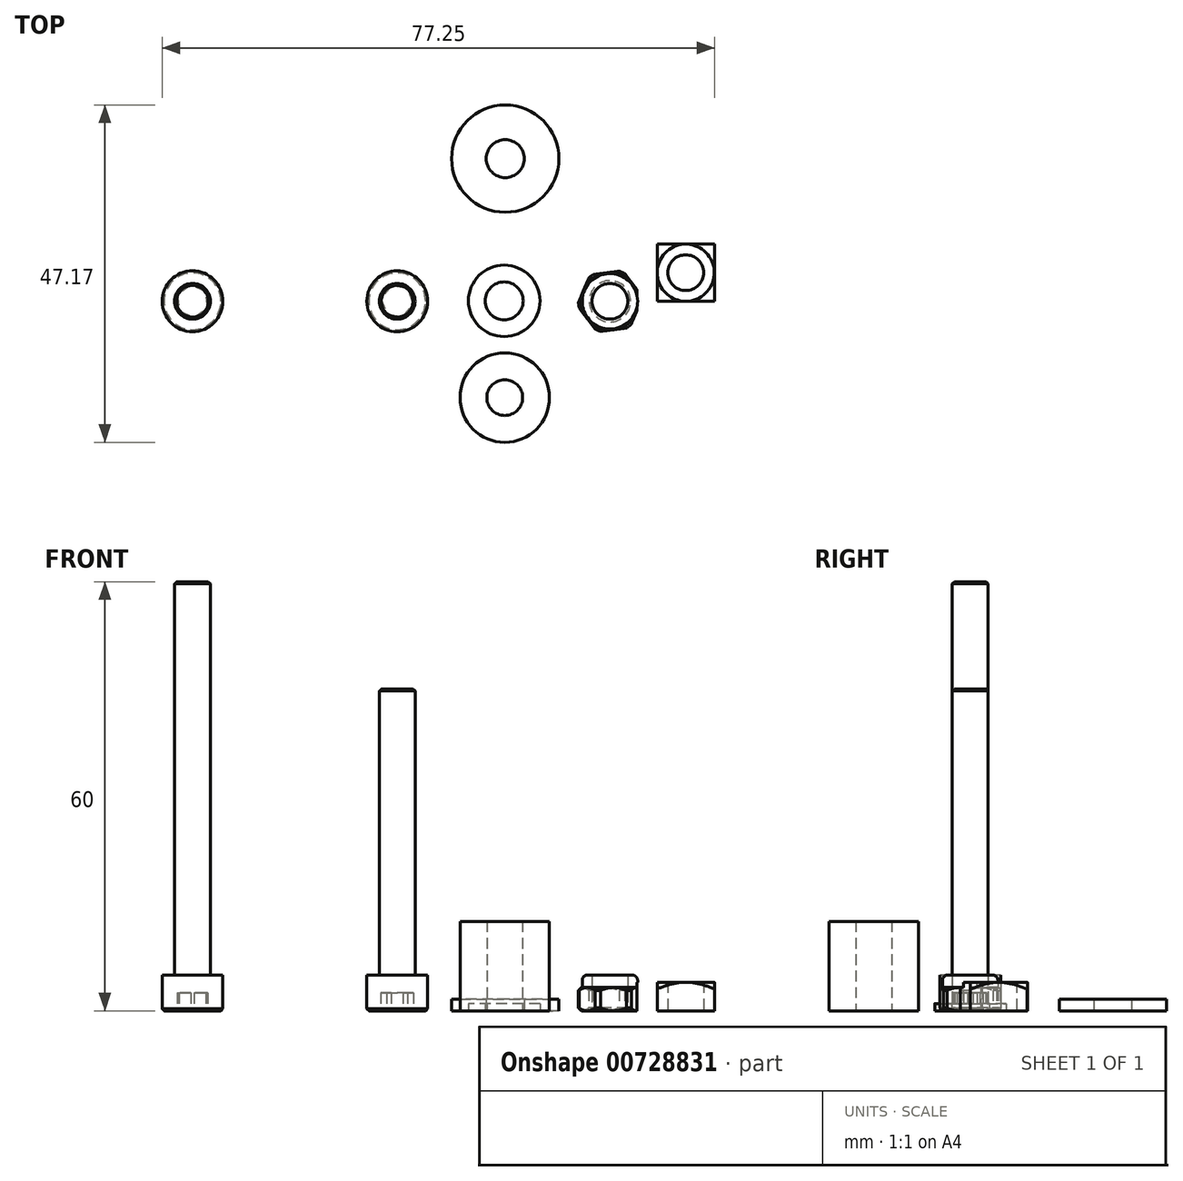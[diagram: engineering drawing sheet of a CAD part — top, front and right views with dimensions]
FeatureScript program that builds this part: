
annotation { "Feature Type Name" : "Feature", "Feature Type Description" : "" }
export const myFeature = defineFeature(function(context is Context, id is Id, definition is map)
    precondition{}
    {
        {
            var Q0;
            Q0=qCreatedBy(makeId("Front.planeOp"),FACE);
            var sketch = newSketch(context, id + "F0", { "sketchPlane" : qUnion([Q0])});
            skLineSegment(sketch, "E0.bottom", {"start": v(-4.25, 5) * mm, "end": v(-2.5, 5) * mm});
            skLineSegment(sketch, "E0.top", {"start": v(-3.97, 0) * mm, "end": v(0, 0) * mm});
            skLineSegment(sketch, "E0.left", {"start": v(-4.25, 5) * mm, "end": v(-4.25, 0.28) * mm});
            skLineSegment(sketch, "E0.right", {"start": v(0, 5) * mm, "end": v(0, 0) * mm});
            skLineSegment(sketch, "E1.top", {"start": v(0, 45) * mm, "end": v(-2.22, 45) * mm});
            skLineSegment(sketch, "E1.left", {"start": v(0, 5) * mm, "end": v(0, 45) * mm});
            skLineSegment(sketch, "E1.right", {"start": v(-2.5, 5) * mm, "end": v(-2.5, 44.72) * mm});
            skLineSegment(sketch, "E2", {"start": v(-4.25, 0.28) * mm, "end": v(-3.97, 0) * mm});
            skLineSegment(sketch, "E3", {"start": v(-2.5, 44.72) * mm, "end": v(-2.22, 45) * mm});
            skSolve(sketch);
        }
        {
            var Q0;
            Q0 = qSketchRegion(id + "F0", true);
            var Q1;
            Q1=sQuery(id+"F0.wireOp",EDGE,"E1.left");
            revolve(context, id + "F1", {"surfaceOperationType" : NewSurfaceOperationType.NEW, "entities" : qUnion([Q0]), "axis" : qUnion([Q1]), "revolveType" : RevolveType.FULL});
        }
        {
            var Q0;
            Q0=makeQuery(id+"F1.opRevolve","SWEPT_FACE",FACE,{"disambiguationData":[OSD([sQuery(id+"F0.wireOp",EDGE,"E0.top")])]});
            var sketch = newSketch(context, id + "F2", { "sketchPlane" : qUnion([Q0])});
            skCircle(sketch, "E4.cCircle", {"center": v(0, 0) * mm, "radius": 2 * mm, "construction": true});
            skLineSegment(sketch, "E4.0", {"start": v(0.82, 2.16) * mm, "end": v(2.28, 0.37) * mm});
            skLineSegment(sketch, "E4.1", {"start": v(2.28, 0.37) * mm, "end": v(1.46, -1.79) * mm});
            skLineSegment(sketch, "E4.2", {"start": v(1.46, -1.79) * mm, "end": v(-0.82, -2.16) * mm});
            skLineSegment(sketch, "E4.3", {"start": v(-0.82, -2.16) * mm, "end": v(-2.28, -0.37) * mm});
            skLineSegment(sketch, "E4.4", {"start": v(-2.28, -0.37) * mm, "end": v(-1.46, 1.79) * mm});
            skLineSegment(sketch, "E4.5", {"start": v(-1.46, 1.79) * mm, "end": v(0.82, 2.16) * mm});
            skPoint(sketch, "E4.0.midPoint", {"position": v(1.55, 1.27) * mm});
            skSolve(sketch);
        }
        {
            var Q0;
            Q0 = qSketchRegion(id + "F2", true);
            extrude(context, id + "F3", {"entities" : qUnion([Q0]), "operationType" : NewBodyOperationType.REMOVE, "oppositeDirection" : true, "depth" : 2.5 * mm, "offsetDistance" : 25 * mm});
        }
        {
            var Q0;
            Q0=qCreatedBy(makeId("Top.planeOp"),FACE);
            var sketch = newSketch(context, id + "F4", { "sketchPlane" : qUnion([Q0])});
            skCircle(sketch, "E5", {"center": v(14.96, 0.06) * mm, "radius": 2.65 * mm});
            skCircle(sketch, "E6", {"center": v(14.96, 0.06) * mm, "radius": 5 * mm});
            skSolve(sketch);
        }
        {
            var Q0;
            Q0 = qSketchRegion(id + "F4", true);
            extrude(context, id + "F5", {"entities" : qUnion([Q0]), "depth" : 1 * mm, "offsetDistance" : 25 * mm});
        }
        {
            var Q0;
            Q0=qCreatedBy(makeId("Top.planeOp"),FACE);
            var sketch = newSketch(context, id + "F6", { "sketchPlane" : qUnion([Q0])});
            skCircle(sketch, "E7", {"center": v(29.74, 0) * mm, "radius": 4.4 * mm});
            skCircle(sketch, "E8", {"center": v(29.74, 0) * mm, "radius": 2.5 * mm});
            skSolve(sketch);
        }
        {
            var Q0;
            Q0 = qSketchRegion(id + "F6", true);
            extrude(context, id + "F7", {"entities" : qUnion([Q0]), "depth" : 3.25 * mm, "offsetDistance" : 25 * mm});
        }
        {
            var Q0;
            Q0=makeQuery(id+"F7.opExtrude","CAP_EDGE",EDGE,{"disambiguationData":[OSD([sQuery(id+"F6.wireOp",EDGE,"E8")])],"isStart":true});
            var Q1;
            Q1=makeQuery(id+"F7.opExtrude","CAP_EDGE",EDGE,{"disambiguationData":[OSD([sQuery(id+"F6.wireOp",EDGE,"E7")])],"isStart":true});
            var Q2;
            Q2=makeQuery(id+"F7.opExtrude","CAP_EDGE",EDGE,{"disambiguationData":[OSD([sQuery(id+"F6.wireOp",EDGE,"E7")])],"isStart":false});
            chamfer(context, id + "F8", {"entities" : qUnion([Q0, Q1, Q2]), "width" : 0.4 * mm, "tangentPropagation" : true});
        }
        {
            var Q0;
            Q0=makeQuery(id+"F7.opExtrude","CAP_FACE",FACE,{"disambiguationData":[OSD([sQuery(id+"F6.wireOp",EDGE,"E7"),sQuery(id+"F6.wireOp",EDGE,"E8")])],"isStart":true});
            var sketch = newSketch(context, id + "F9", { "sketchPlane" : qUnion([Q0])});
            skCircle(sketch, "E9.cCircle", {"center": v(29.74, 0) * mm, "radius": 4 * mm, "construction": true});
            skLineSegment(sketch, "E9.0", {"start": v(25.16, 0.58) * mm, "end": v(27.95, 4.26) * mm});
            skLineSegment(sketch, "E9.1", {"start": v(27.95, 4.26) * mm, "end": v(32.54, 3.68) * mm});
            skLineSegment(sketch, "E9.2", {"start": v(32.54, 3.68) * mm, "end": v(34.32, -0.58) * mm});
            skLineSegment(sketch, "E9.3", {"start": v(34.32, -0.58) * mm, "end": v(31.52, -4.26) * mm});
            skLineSegment(sketch, "E9.4", {"start": v(31.52, -4.26) * mm, "end": v(26.94, -3.68) * mm});
            skLineSegment(sketch, "E9.5", {"start": v(26.94, -3.68) * mm, "end": v(25.16, 0.58) * mm});
            skPoint(sketch, "E9.0.midPoint", {"position": v(26.56, 2.42) * mm});
            skCircle(sketch, "E10", {"center": v(29.74, 0) * mm, "radius": 6.63 * mm});
            skSolve(sketch);
        }
        {
            var Q0;
            Q0 = qSketchRegion(id + "F9", true);
            extrude(context, id + "F10", {"entities" : qUnion([Q0]), "operationType" : NewBodyOperationType.REMOVE, "oppositeDirection" : true, "depth" : 25 * mm, "offsetDistance" : 25 * mm});
        }
        {
            var Q0;
            Q0=makeQuery(id+"F7.opExtrude","CAP_FACE",FACE,{"disambiguationData":[OSD([sQuery(id+"F6.wireOp",EDGE,"E7"),sQuery(id+"F6.wireOp",EDGE,"E8")])],"isStart":false});
            var sketch = newSketch(context, id + "F11", { "sketchPlane" : qUnion([Q0])});
            skCircle(sketch, "E11", {"center": v(29.74, 0) * mm, "radius": 2.5 * mm});
            skCircle(sketch, "E12", {"center": v(29.74, 0) * mm, "radius": 3.88 * mm});
            skSolve(sketch);
        }
        {
            var Q0;
            Q0 = qSketchRegion(id + "F11", true);
            extrude(context, id + "F12", {"entities" : qUnion([Q0]), "operationType" : NewBodyOperationType.ADD, "depth" : 1.75 * mm, "offsetDistance" : 25 * mm});
        }
        {
            var Q0;
            Q0=makeQuery(id+"F12.opExtrude","CAP_EDGE",EDGE,{"disambiguationData":[OSD([sQuery(id+"F11.wireOp",EDGE,"E12")])],"isStart":false});
            fillet(context, id + "F13", {"entities" : qUnion([Q0]), "radius" : 0.75 * mm, "tangentPropagation" : true, "allowEdgeOverflow" : false});
        }
        {
            var Q0;
            Q0=qCreatedBy(makeId("Top.planeOp"),FACE);
            var sketch = newSketch(context, id + "F14", { "sketchPlane" : qUnion([Q0])});
            skLineSegment(sketch, "E13.bottom", {"start": v(36.34, 8) * mm, "end": v(44.34, 8) * mm, "construction": true});
            skLineSegment(sketch, "E13.top", {"start": v(36.34, 0) * mm, "end": v(44.34, 0) * mm, "construction": true});
            skLineSegment(sketch, "E13.left", {"start": v(36.34, 8) * mm, "end": v(36.34, 0) * mm, "construction": true});
            skLineSegment(sketch, "E13.right", {"start": v(44.34, 8) * mm, "end": v(44.34, 0) * mm, "construction": true});
            skCircle(sketch, "E14", {"center": v(40.34, 4) * mm, "radius": 2.5 * mm});
            skPoint(sketch, "E14.centerSnap0", {"position": v(40.34, 8) * mm});
            skPoint(sketch, "E14.centerSnap1", {"position": v(36.34, 4) * mm});
            skCircle(sketch, "E15", {"center": v(40.34, 4) * mm, "radius": 5.66 * mm});
            skSolve(sketch);
        }
        {
            var Q0;
            Q0 = qSketchRegion(id + "F14", true);
            extrude(context, id + "F15", {"entities" : qUnion([Q0]), "depth" : 4 * mm, "offsetDistance" : 25 * mm});
        }
        {
            var Q0;
            Q0=makeQuery(id+"F15.opExtrude","CAP_EDGE",EDGE,{"disambiguationData":[OSD([sQuery(id+"F14.wireOp",EDGE,"E15")])],"isStart":false});
            chamfer(context, id + "F16", {"entities" : qUnion([Q0]), "chamferType" : ChamferType.OFFSET_ANGLE, "width" : 1.67 * mm, "oppositeDirection" : false, "angle" : 30 * degree, "tangentPropagation" : true});
        }
        {
            var Q0;
            Q0=makeQuery(id+"F15.opExtrude","CAP_FACE",FACE,{"disambiguationData":[OSD([sQuery(id+"F14.wireOp",EDGE,"E14"),sQuery(id+"F14.wireOp",EDGE,"E15")])],"isStart":false});
            var sketch = newSketch(context, id + "F17", { "sketchPlane" : qUnion([Q0])});
            skLineSegment(sketch, "E16.bottom", {"start": v(36.38, 8.04) * mm, "end": v(44.38, 8.04) * mm});
            skLineSegment(sketch, "E16.top", {"start": v(36.38, 0.04) * mm, "end": v(44.38, 0.04) * mm});
            skLineSegment(sketch, "E16.left", {"start": v(36.38, 8.04) * mm, "end": v(36.38, 0.04) * mm});
            skLineSegment(sketch, "E16.right", {"start": v(44.38, 8.04) * mm, "end": v(44.38, 0.04) * mm});
            skLineSegment(sketch, "E17.bottom", {"start": v(33.5, 11.67) * mm, "end": v(48.64, 11.67) * mm});
            skLineSegment(sketch, "E17.top", {"start": v(33.5, -3.63) * mm, "end": v(48.64, -3.63) * mm});
            skLineSegment(sketch, "E17.left", {"start": v(33.5, 11.67) * mm, "end": v(33.5, -3.63) * mm});
            skLineSegment(sketch, "E17.right", {"start": v(48.64, 11.67) * mm, "end": v(48.64, -3.63) * mm});
            skSolve(sketch);
        }
        {
            var Q0;
            Q0 = qSketchRegion(id + "F17", true);
            extrude(context, id + "F18", {"entities" : qUnion([Q0]), "operationType" : NewBodyOperationType.REMOVE, "endBound" : BoundingType.THROUGH_ALL, "oppositeDirection" : true, "depth" : 25 * mm, "offsetDistance" : 25 * mm});
        }
        {
            var Q0;
            Q0=qCreatedBy(makeId("Front.planeOp"),FACE);
            var sketch = newSketch(context, id + "F19", { "sketchPlane" : qUnion([Q0])});
            skLineSegment(sketch, "E18.bottom", {"start": v(-32.87, 5) * mm, "end": v(-31.12, 5) * mm});
            skLineSegment(sketch, "E18.top", {"start": v(-32.58, 0) * mm, "end": v(-28.62, 0) * mm});
            skLineSegment(sketch, "E18.left", {"start": v(-32.87, 5) * mm, "end": v(-32.87, 0.28) * mm});
            skLineSegment(sketch, "E18.right", {"start": v(-28.62, 5) * mm, "end": v(-28.62, 0) * mm});
            skLineSegment(sketch, "E19.top", {"start": v(-28.62, 60) * mm, "end": v(-30.83, 60) * mm});
            skLineSegment(sketch, "E19.left", {"start": v(-28.62, 5) * mm, "end": v(-28.62, 60) * mm});
            skLineSegment(sketch, "E19.right", {"start": v(-31.12, 5) * mm, "end": v(-31.12, 59.72) * mm});
            skLineSegment(sketch, "E20", {"start": v(-32.87, 0.28) * mm, "end": v(-32.58, 0) * mm});
            skLineSegment(sketch, "E21", {"start": v(-31.12, 59.72) * mm, "end": v(-30.83, 60) * mm});
            skSolve(sketch);
        }
        {
            var Q0;
            Q0 = qSketchRegion(id + "F19", true);
            var Q1;
            Q1=sQuery(id+"F19.wireOp",EDGE,"E19.left");
            revolve(context, id + "F20", {"surfaceOperationType" : NewSurfaceOperationType.NEW, "entities" : qUnion([Q0]), "axis" : qUnion([Q1]), "revolveType" : RevolveType.FULL});
        }
        {
            var Q0;
            Q0=makeQuery(id+"F20.opRevolve","SWEPT_FACE",FACE,{"disambiguationData":[OSD([sQuery(id+"F19.wireOp",EDGE,"E18.top")])]});
            var sketch = newSketch(context, id + "F21", { "sketchPlane" : qUnion([Q0])});
            skCircle(sketch, "E22.cCircle", {"center": v(-28.62, 0) * mm, "radius": 2 * mm, "construction": true});
            skLineSegment(sketch, "E22.0", {"start": v(-28.38, 2.3) * mm, "end": v(-26.51, 0.95) * mm});
            skLineSegment(sketch, "E22.1", {"start": v(-26.51, 0.95) * mm, "end": v(-26.74, -1.35) * mm});
            skLineSegment(sketch, "E22.2", {"start": v(-26.74, -1.35) * mm, "end": v(-28.85, -2.3) * mm});
            skLineSegment(sketch, "E22.3", {"start": v(-28.85, -2.3) * mm, "end": v(-30.72, -0.95) * mm});
            skLineSegment(sketch, "E22.4", {"start": v(-30.72, -0.95) * mm, "end": v(-30.49, 1.35) * mm});
            skLineSegment(sketch, "E22.5", {"start": v(-30.49, 1.35) * mm, "end": v(-28.38, 2.3) * mm});
            skPoint(sketch, "E22.0.midPoint", {"position": v(-27.45, 1.62) * mm});
            skSolve(sketch);
        }
        {
            var Q0;
            Q0 = qSketchRegion(id + "F21", true);
            extrude(context, id + "F22", {"entities" : qUnion([Q0]), "operationType" : NewBodyOperationType.REMOVE, "oppositeDirection" : true, "depth" : 2.5 * mm, "offsetDistance" : 25 * mm});
        }
        {
            var Q0;
            Q0=qCreatedBy(makeId("Top.planeOp"),FACE);
            var sketch = newSketch(context, id + "F23", { "sketchPlane" : qUnion([Q0])});
            skCircle(sketch, "E23", {"center": v(15.04, -13.47) * mm, "radius": 2.5 * mm});
            skCircle(sketch, "E24", {"center": v(15.04, -13.47) * mm, "radius": 6.25 * mm});
            skSolve(sketch);
        }
        {
            var Q0;
            Q0 = qSketchRegion(id + "F23", true);
            extrude(context, id + "F24", {"entities" : qUnion([Q0]), "depth" : 12.5 * mm, "offsetDistance" : 25 * mm});
        }
        {
            var Q0;
            Q0=qCreatedBy(makeId("Top.planeOp"),FACE);
            var sketch = newSketch(context, id + "F25", { "sketchPlane" : qUnion([Q0])});
            skCircle(sketch, "E25", {"center": v(15.1, 19.95) * mm, "radius": 2.65 * mm});
            skCircle(sketch, "E26", {"center": v(15.1, 19.95) * mm, "radius": 7.5 * mm});
            skSolve(sketch);
        }
        {
            var Q0;
            Q0 = qSketchRegion(id + "F25", true);
            extrude(context, id + "F26", {"entities" : qUnion([Q0]), "depth" : 1.6 * mm, "offsetDistance" : 25 * mm});
        }
    });
